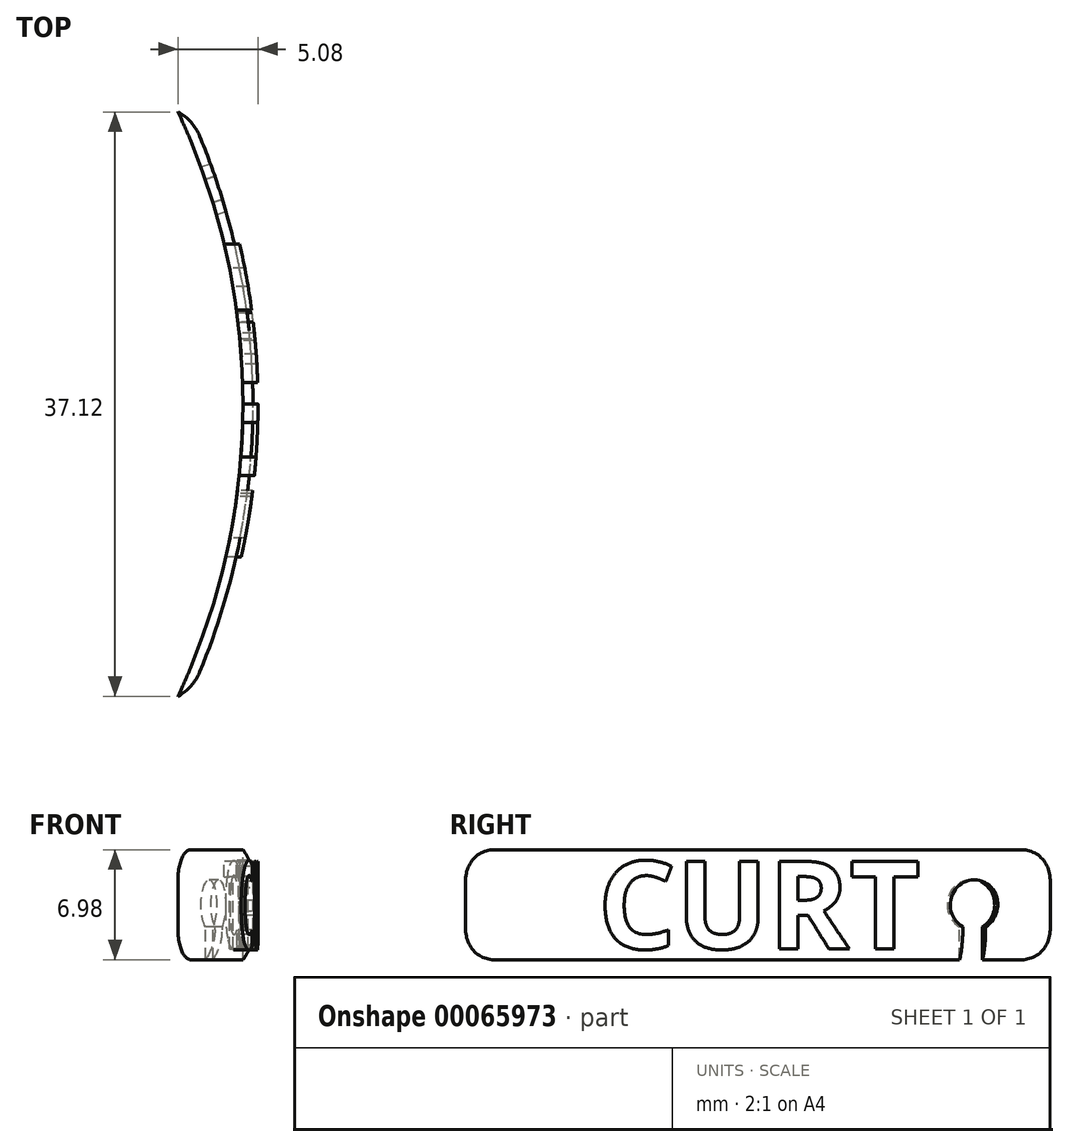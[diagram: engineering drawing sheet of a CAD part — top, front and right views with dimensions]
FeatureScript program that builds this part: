
annotation { "Feature Type Name" : "Feature", "Feature Type Description" : "" }
export const myFeature = defineFeature(function(context is Context, id is Id, definition is map)
    precondition{}
    {
        {
            var Q0;
            Q0=qCreatedBy(makeId("Front.planeOp"),FACE);
            var sketch = newSketch(context, id + "F0", { "sketchPlane" : qUnion([Q0])});
            skLineSegment(sketch, "E0", {"start": v(38.1, -1.59) * mm, "end": v(38.1, 1.59) * mm});
            skLineSegment(sketch, "E1", {"start": v(44.45, 1.59) * mm, "end": v(44.45, -1.59) * mm});
            skArc(sketch, "E2", {"start": v(44.45, 1.59) * mm, "mid": v(41.28, 4.76) * mm, "end": v(38.1, 1.59) * mm});
            skArc(sketch, "E3", {"start": v(38.1, -1.59) * mm, "mid": v(41.28, -4.76) * mm, "end": v(44.45, -1.59) * mm});
            skLineSegment(sketch, "E4", {"start": v(0, 0) * mm, "end": v(0, -27.8) * mm});
            skSolve(sketch);
        }
        {
            var Q0;
            Q0=makeQuery(id+"F0.imprint","IMPRINT",FACE,{"disambiguationData":[TD([[makeQuery(id+"F0.imprint","IMPRINT",EDGE,{"derivedFrom":sQuery(id+"F0.wireOp",EDGE,"E0")}),-1.0]])]});
            var Q1;
            Q1=sQuery(id+"F0.wireOp",EDGE,"E4");
            revolve(context, id + "F1", {"entities" : qUnion([Q0]), "axis" : qUnion([Q1]), "revolveType" : RevolveType.SYMMETRIC, "angle" : 45 * degree});
        }
        {
            var Q0;
            Q0=makeQuery(id+"F1.opRevolve","CAP_FACE",FACE,{"disambiguationData":[OSD([sQuery(id+"F0.wireOp",EDGE,"E0"),sQuery(id+"F0.wireOp",EDGE,"E1"),sQuery(id+"F0.wireOp",EDGE,"E2"),sQuery(id+"F0.wireOp",EDGE,"E3")])],"isStart":false});
            var sketch = newSketch(context, id + "F2", { "sketchPlane" : qUnion([Q0])});
            skLineSegment(sketch, "E5", {"start": v(41.28, 4.76) * mm, "end": v(41.28, -4.76) * mm});
            skSolve(sketch);
        }
        {
            var Q0;
            Q0 = qSketchRegion(id + "F2", true);
            var Q1;
            {var subQ0=sQuery(id+"F2.wireOp",EDGE,"E5");Q1=makeQuery(id+"F2.imprint","IMPRINT",FACE,{"disambiguationData":[TD([[makeQuery(id+"F2.imprint","IMPRINT",EDGE,{"derivedFrom":subQ0}),1.0]])]});}
            var Q2;
            Q2=sQuery(id+"F2.wireOp",EDGE,"E5");
            revolve(context, id + "F3", {"operationType" : NewBodyOperationType.ADD, "entities" : qUnion([Q0, Q1]), "axis" : qUnion([Q2]), "revolveType" : RevolveType.FULL});
        }
        {
            var Q0;
            Q0=makeQuery(id+"F1.opRevolve","CAP_FACE",FACE,{"disambiguationData":[OSD([sQuery(id+"F0.wireOp",EDGE,"E0"),sQuery(id+"F0.wireOp",EDGE,"E1"),sQuery(id+"F0.wireOp",EDGE,"E2"),sQuery(id+"F0.wireOp",EDGE,"E3")])],"isStart":true});
            var sketch = newSketch(context, id + "F4", { "sketchPlane" : qUnion([Q0])});
            skLineSegment(sketch, "E6", {"start": v(-41.28, 4.76) * mm, "end": v(-41.28, -4.76) * mm});
            skSolve(sketch);
        }
        {
            var Q0;
            Q0 = qSketchRegion(id + "F4", true);
            var Q1;
            {var subQ0=sQuery(id+"F4.wireOp",EDGE,"E6");Q1=makeQuery(id+"F4.imprint","IMPRINT",FACE,{"disambiguationData":[TD([[makeQuery(id+"F4.imprint","IMPRINT",EDGE,{"derivedFrom":subQ0}),1.0]])]});}
            var Q2;
            Q2=sQuery(id+"F4.wireOp",EDGE,"E6");
            revolve(context, id + "F5", {"operationType" : NewBodyOperationType.ADD, "entities" : qUnion([Q0, Q1]), "axis" : qUnion([Q2]), "revolveType" : RevolveType.FULL});
        }
        {
            var Q0;
            Q0=qCreatedBy(makeId("Front.planeOp"),FACE);
            var sketch = newSketch(context, id + "F6", { "sketchPlane" : qUnion([Q0])});
            skLineSegment(sketch, "E7", {"start": v(38.13, 4.76) * mm, "end": v(41.28, 4.76) * mm});
            skArc(sketch, "E8", {"start": v(41.28, 4.76) * mm, "mid": v(39.03, 3.83) * mm, "end": v(38.1, 1.59) * mm});
            skLineSegment(sketch, "E9", {"start": v(44.45, 1.59) * mm, "end": v(44.45, -1.59) * mm});
            skLineSegment(sketch, "E10", {"start": v(38.13, -4.76) * mm, "end": v(41.28, -4.76) * mm});
            skArc(sketch, "E11", {"start": v(38.1, -1.59) * mm, "mid": v(39.03, -3.83) * mm, "end": v(41.28, -4.76) * mm});
            skLineSegment(sketch, "E12", {"start": v(41.28, 4.76) * mm, "end": v(41.28, -4.76) * mm, "construction": true});
            skLineSegment(sketch, "E13", {"start": v(0, 0) * mm, "end": v(48.62, 0) * mm, "construction": true});
            skPoint(sketch, "E13.endSnap0", {"position": v(44.45, 0) * mm});
            skLineSegment(sketch, "E14", {"start": v(39.69, -6.35) * mm, "end": v(39.69, 0.76) * mm});
            skLineSegment(sketch, "E15", {"start": v(42.86, -6.35) * mm, "end": v(42.86, 0.76) * mm});
            skLineSegment(sketch, "E16", {"start": v(39.69, -6.35) * mm, "end": v(42.86, -6.35) * mm});
            skArc(sketch, "E17", {"start": v(42.86, 0.76) * mm, "mid": v(41.28, 2.35) * mm, "end": v(39.69, 0.76) * mm});
            skLineSegment(sketch, "E18", {"start": v(0, 0) * mm, "end": v(0, -11.33) * mm, "construction": true});
            skArc(sketch, "E19", {"start": v(39.69, -4.28) * mm, "mid": v(40, -2.76) * mm, "end": v(39.69, -1.23) * mm});
            skArc(sketch, "E20", {"start": v(42.86, -1.23) * mm, "mid": v(42.55, -2.76) * mm, "end": v(42.86, -4.28) * mm});
            skLineSegment(sketch, "E21", {"start": v(39.69, -1.23) * mm, "end": v(42.86, -1.23) * mm, "construction": true});
            skLineSegment(sketch, "E22", {"start": v(39.69, -4.28) * mm, "end": v(42.86, -4.28) * mm, "construction": true});
            skSolve(sketch);
        }
        {
            var Q0;
            {var subQ0=sQuery(id+"F6.wireOp",EDGE,"E11");var subQ1=sQuery(id+"F6.wireOp",EDGE,"E10");var subQ2=makeQuery(id+"F6.imprint","INTERSECT",VERTEX,{"derivedFrom":[subQ1,subQ0]});Q0=makeQuery(id+"F6.imprint","IMPRINT",FACE,{"disambiguationData":[TD([[makeQuery(id+"F6.imprint","IMPRINT",EDGE,{"disambiguationData":[TD([[subQ2,1.0]])],"derivedFrom":subQ1}),1.0]])]});}
            var Q1;
            Q1=makeQuery(id+"F6.imprint","IMPRINT",FACE,{"disambiguationData":[TD([[makeQuery(id+"F6.imprint","IMPRINT",EDGE,{"derivedFrom":sQuery(id+"F6.wireOp",EDGE,"E15")}),1.0]])]});
            var Q2;
            Q2=sQuery(id+"F6.wireOp",EDGE,"E18");
            revolve(context, id + "F7", {"operationType" : NewBodyOperationType.REMOVE, "entities" : qUnion([Q0, Q1]), "axis" : qUnion([Q2]), "revolveType" : RevolveType.FULL, "oppositeDirection" : true});
        }
        {
            var Q0;
            Q0=qCreatedBy(makeId("Top.planeOp"),FACE);
            var sketch = newSketch(context, id + "F8", { "sketchPlane" : qUnion([Q0])});
            skArc(sketch, "E23.0", {"start": v(41.07, -17.01) * mm, "mid": v(44.45, 0) * mm, "end": v(41.07, 17.01) * mm});
            skLineSegment(sketch, "E24.0", {"start": v(41.07, 17.01) * mm, "end": v(35.2, 14.58) * mm});
            skFitSpline(sketch, "E25.0", {"points": [v(35.7, 17.84) * mm, v(35.8, 17.96) * mm, v(35.96, 18.09) * mm, v(36.16, 18.22) * mm, v(36.37, 18.36) * mm, v(36.6, 18.48) * mm, v(36.85, 18.6) * mm, v(37.1, 18.72) * mm, v(37.35, 18.8) * mm, v(37.59, 18.87) * mm, v(37.82, 18.94) * mm, v(38.02, 18.97) * mm, v(38.18, 18.97) * mm]});
            skPoint(sketch, "E26.startSnap0", {"position": v(38.13, 15.8) * mm});
            skCircle(sketch, "E27", {"center": v(0, 0) * mm, "radius": 41.28 * mm, "construction": true});
            skLineSegment(sketch, "E28", {"start": v(0, 0) * mm, "end": v(47.07, 15.3) * mm, "construction": true});
            skArc(sketch, "E29", {"start": v(38.53, 12.52) * mm, "mid": v(37.01, 16.48) * mm, "end": v(35.09, 20.26) * mm});
            skArc(sketch, "E30", {"start": v(39.98, 13) * mm, "mid": v(38.4, 17.1) * mm, "end": v(36.4, 21.02) * mm});
            skArc(sketch, "E31", {"start": v(38.53, 12.52) * mm, "mid": v(39.5, 12.03) * mm, "end": v(39.98, 13) * mm});
            skLineSegment(sketch, "E32", {"start": v(35.09, 20.26) * mm, "end": v(36.4, 21.02) * mm});
            skSolve(sketch);
        }
        {
            var Q0;
            Q0 = qSketchRegion(id + "F8", true);
            extrude(context, id + "F9", {"entities" : qUnion([Q0]), "operationType" : NewBodyOperationType.REMOVE, "endBound" : BoundingType.THROUGH_ALL, "depth" : 25.4 * mm});
        }
        {
            var Q0;
            Q0=sQuery(id+"F8.wireOp",VERTEX,"E30.center");
            var Q1;
            Q1=sQuery(id+"F8.wireOp",EDGE,"E28");
            cPlane(context, id + "F10", {"entities" : qUnion([Q0, Q1]), "cplaneType" : CPlaneType.LINE_POINT, "offset" : 152.4 * mm, "width" : 152.4 * mm, "height" : 152.4 * mm});
        }
        {
            var Q0;
            Q0=qCreatedBy(id+"F10.planeOp",FACE);
            var sketch = newSketch(context, id + "F11", { "sketchPlane" : qUnion([Q0])});
            skPoint(sketch, "E33", {"position": v(0, 0) * mm});
            skSolve(sketch);
        }
        {
            var Q0;
            Q0=sQuery(id+"F11.wireOp",VERTEX,"E33");
            var Q1;
            Q1=makeQuery(id+"F1.opRevolve","SWEPT_BODY",BODY,{"disambiguationData":[OSD([sQuery(id+"F0.wireOp",EDGE,"E0"),sQuery(id+"F0.wireOp",EDGE,"E1"),sQuery(id+"F0.wireOp",EDGE,"E2"),sQuery(id+"F0.wireOp",EDGE,"E3")])]});
            hole(context, id + "F12", {"style" : HoleStyle.SIMPLE, "holeDiameter" : 3.17 * mm, "endStyle" : HoleEndStyle.THROUGH, "oppositeDirection" : true, "locations" : qUnion([Q0]), "scope" : qUnion([Q1])});
        }
        {
            var Q0;
            Q0=qCreatedBy(makeId("Top.planeOp"),FACE);
            var sketch = newSketch(context, id + "F13", { "sketchPlane" : qUnion([Q0])});
            skArc(sketch, "E34.0", {"start": v(38.53, 12.52) * mm, "mid": v(39.5, 12.03) * mm, "end": v(39.98, 13) * mm});
            skLineSegment(sketch, "E35", {"start": v(40.25, 14.75) * mm, "end": v(41.76, 15.24) * mm});
            skLineSegment(sketch, "E36", {"start": v(42.74, 12.22) * mm, "end": v(41.23, 11.73) * mm});
            skLineSegment(sketch, "E37", {"start": v(35.71, 13.27) * mm, "end": v(37.22, 13.76) * mm});
            skLineSegment(sketch, "E38", {"start": v(38.2, 10.74) * mm, "end": v(36.7, 10.25) * mm});
            skLineSegment(sketch, "E39", {"start": v(35.4, 12.3) * mm, "end": v(39.02, 13.48) * mm});
            skLineSegment(sketch, "E40", {"start": v(39.02, 13.48) * mm, "end": v(39.5, 12.03) * mm});
            skLineSegment(sketch, "E41", {"start": v(39.5, 12.03) * mm, "end": v(35.86, 10.85) * mm});
            skLineSegment(sketch, "E42", {"start": v(35.86, 10.85) * mm, "end": v(35.4, 12.3) * mm});
            skLineSegment(sketch, "E43", {"start": v(35.63, 11.58) * mm, "end": v(39.25, 12.75) * mm, "construction": true});
            skSolve(sketch);
        }
        {
            var Q0;
            Q0 = qSketchRegion(id + "F13", true);
            extrude(context, id + "F14", {"entities" : qUnion([Q0]), "operationType" : NewBodyOperationType.REMOVE, "endBound" : BoundingType.THROUGH_ALL, "depth" : 25.4 * mm});
        }
        {
            var Q0;
            Q0=qCreatedBy(makeId("Top.planeOp"),FACE);
            var sketch = newSketch(context, id + "F15", { "sketchPlane" : qUnion([Q0])});
            skLineSegment(sketch, "E44", {"start": v(39.02, 13.48) * mm, "end": v(39.5, 12.03) * mm});
            skLineSegment(sketch, "E45", {"start": v(39.5, 12.03) * mm, "end": v(43.11, 13.2) * mm});
            skLineSegment(sketch, "E46", {"start": v(43.11, 13.2) * mm, "end": v(42.64, 14.66) * mm});
            skLineSegment(sketch, "E47", {"start": v(42.64, 14.66) * mm, "end": v(39.02, 13.48) * mm});
            skSolve(sketch);
        }
        {
            var Q0;
            Q0 = qSketchRegion(id + "F15", true);
            extrude(context, id + "F16", {"entities" : qUnion([Q0]), "operationType" : NewBodyOperationType.REMOVE, "endBound" : BoundingType.THROUGH_ALL, "oppositeDirection" : true, "depth" : 25.4 * mm});
        }
        {
            var Q0;
            {var subQ0=sQuery(id+"F0.wireOp",EDGE,"E3");var subQ1=makeQuery(id+"F1.opRevolve","SWEPT_FACE",FACE,{"disambiguationData":[OSD([subQ0])]});var subQ2=sQuery(id+"F6.wireOp",EDGE,"E15");var subQ3=makeQuery(id+"F7.opRevolve","SWEPT_FACE",FACE,{"disambiguationData":[OSD([subQ2]),TDD([makeQuery(id+"F6.imprint","IMPRINT",EDGE,{"disambiguationData":[TD([[makeQuery(id+"F6.imprint","INTERSECT",VERTEX,{"derivedFrom":[subQ2,sQuery(id+"F6.wireOp",EDGE,"E16")]}),-1.0]])],"derivedFrom":subQ2})])]});Q0=makeQuery(id+"F16.boolean.opBoolean","SPLIT",EDGE,{"disambiguationData":[TD([makeQuery(id+"F3.opRevolve","SWEPT_FACE",FACE,{"disambiguationData":[OSD([subQ0])]})])],"derivedFrom":makeQuery(id+"F7.boolean.opBoolean","INTERSECT",EDGE,{"derivedFrom":[subQ1,subQ3]})});}
            var Q1;
            {var subQ0=sQuery(id+"F0.wireOp",EDGE,"E3");var subQ1=makeQuery(id+"F1.opRevolve","SWEPT_FACE",FACE,{"disambiguationData":[OSD([subQ0])]});var subQ2=sQuery(id+"F6.wireOp",EDGE,"E15");var subQ3=makeQuery(id+"F7.opRevolve","SWEPT_FACE",FACE,{"disambiguationData":[OSD([subQ2]),TDD([makeQuery(id+"F6.imprint","IMPRINT",EDGE,{"disambiguationData":[TD([[makeQuery(id+"F6.imprint","INTERSECT",VERTEX,{"derivedFrom":[subQ2,sQuery(id+"F6.wireOp",EDGE,"E16")]}),-1.0]])],"derivedFrom":subQ2})])]});Q1=makeQuery(id+"F16.boolean.opBoolean","SPLIT",EDGE,{"disambiguationData":[TD([makeQuery(id+"F5.opRevolve","SWEPT_FACE",FACE,{"disambiguationData":[OSD([subQ0])]})])],"derivedFrom":makeQuery(id+"F7.boolean.opBoolean","INTERSECT",EDGE,{"derivedFrom":[subQ1,subQ3]})});}
            var Q2;
            {var subQ0=sQuery(id+"F6.wireOp",EDGE,"E15");Q2=makeQuery(id+"F7.boolean.opBoolean","INTERSECT",EDGE,{"derivedFrom":[makeQuery(id+"F5.opRevolve","SWEPT_FACE",FACE,{"disambiguationData":[OSD([sQuery(id+"F0.wireOp",EDGE,"E3")])]}),makeQuery(id+"F7.opRevolve","SWEPT_FACE",FACE,{"disambiguationData":[OSD([subQ0]),TDD([makeQuery(id+"F6.imprint","IMPRINT",EDGE,{"disambiguationData":[TD([[makeQuery(id+"F6.imprint","INTERSECT",VERTEX,{"derivedFrom":[subQ0,sQuery(id+"F6.wireOp",EDGE,"E16")]}),-1.0]])],"derivedFrom":subQ0})])]})]});}
            var Q3;
            {var subQ0=sQuery(id+"F6.wireOp",EDGE,"E14");var subQ2=makeQuery(id+"F6.imprint","INTERSECT",VERTEX,{"derivedFrom":[sQuery(id+"F6.wireOp",EDGE,"E10"),subQ0]});Q3=makeQuery(id+"F7.boolean.opBoolean","INTERSECT",EDGE,{"derivedFrom":[makeQuery(id+"F5.opRevolve","SWEPT_FACE",FACE,{"disambiguationData":[OSD([sQuery(id+"F0.wireOp",EDGE,"E3")])]}),makeQuery(id+"F7.opRevolve","SWEPT_FACE",FACE,{"disambiguationData":[OSD([subQ0]),TDD([makeQuery(id+"F6.imprint","IMPRINT",EDGE,{"disambiguationData":[TD([[makeQuery(id+"F6.imprint","INTERSECT",VERTEX,{"derivedFrom":[subQ0,sQuery(id+"F6.wireOp",EDGE,"E16")]}),-1.0]])],"derivedFrom":subQ0}),makeQuery(id+"F6.imprint","IMPRINT",EDGE,{"disambiguationData":[TD([[subQ2,-1.0]])],"derivedFrom":subQ0}),makeQuery(id+"F6.imprint","IMPRINT",EDGE,{"disambiguationData":[TD([[makeQuery(id+"F6.imprint","INTERSECT",VERTEX,{"disambiguationData":[OD(0.0)],"derivedFrom":[subQ0,sQuery(id+"F6.wireOp",EDGE,"E19")]}),1.0]])],"derivedFrom":subQ0})])]})]});}
            var Q4;
            {var subQ0=sQuery(id+"F6.wireOp",EDGE,"E14");var subQ2=makeQuery(id+"F6.imprint","INTERSECT",VERTEX,{"derivedFrom":[sQuery(id+"F6.wireOp",EDGE,"E10"),subQ0]});Q4=makeQuery(id+"F7.boolean.opBoolean","INTERSECT",EDGE,{"derivedFrom":[makeQuery(id+"F1.opRevolve","SWEPT_FACE",FACE,{"disambiguationData":[OSD([sQuery(id+"F0.wireOp",EDGE,"E3")])]}),makeQuery(id+"F7.opRevolve","SWEPT_FACE",FACE,{"disambiguationData":[OSD([subQ0]),TDD([makeQuery(id+"F6.imprint","IMPRINT",EDGE,{"disambiguationData":[TD([[makeQuery(id+"F6.imprint","INTERSECT",VERTEX,{"derivedFrom":[subQ0,sQuery(id+"F6.wireOp",EDGE,"E16")]}),-1.0]])],"derivedFrom":subQ0}),makeQuery(id+"F6.imprint","IMPRINT",EDGE,{"disambiguationData":[TD([[subQ2,-1.0]])],"derivedFrom":subQ0}),makeQuery(id+"F6.imprint","IMPRINT",EDGE,{"disambiguationData":[TD([[makeQuery(id+"F6.imprint","INTERSECT",VERTEX,{"disambiguationData":[OD(0.0)],"derivedFrom":[subQ0,sQuery(id+"F6.wireOp",EDGE,"E19")]}),1.0]])],"derivedFrom":subQ0})])]})]});}
            var Q5;
            {var subQ0=sQuery(id+"F6.wireOp",EDGE,"E14");var subQ2=makeQuery(id+"F6.imprint","INTERSECT",VERTEX,{"derivedFrom":[sQuery(id+"F6.wireOp",EDGE,"E10"),subQ0]});Q5=makeQuery(id+"F7.boolean.opBoolean","INTERSECT",EDGE,{"derivedFrom":[makeQuery(id+"F3.opRevolve","SWEPT_FACE",FACE,{"disambiguationData":[OSD([sQuery(id+"F0.wireOp",EDGE,"E3")])]}),makeQuery(id+"F7.opRevolve","SWEPT_FACE",FACE,{"disambiguationData":[OSD([subQ0]),TDD([makeQuery(id+"F6.imprint","IMPRINT",EDGE,{"disambiguationData":[TD([[makeQuery(id+"F6.imprint","INTERSECT",VERTEX,{"derivedFrom":[subQ0,sQuery(id+"F6.wireOp",EDGE,"E16")]}),-1.0]])],"derivedFrom":subQ0}),makeQuery(id+"F6.imprint","IMPRINT",EDGE,{"disambiguationData":[TD([[subQ2,-1.0]])],"derivedFrom":subQ0}),makeQuery(id+"F6.imprint","IMPRINT",EDGE,{"disambiguationData":[TD([[makeQuery(id+"F6.imprint","INTERSECT",VERTEX,{"disambiguationData":[OD(0.0)],"derivedFrom":[subQ0,sQuery(id+"F6.wireOp",EDGE,"E19")]}),1.0]])],"derivedFrom":subQ0})])]})]});}
            var Q6;
            {var subQ0=sQuery(id+"F6.wireOp",EDGE,"E15");Q6=makeQuery(id+"F7.boolean.opBoolean","INTERSECT",EDGE,{"derivedFrom":[makeQuery(id+"F3.opRevolve","SWEPT_FACE",FACE,{"disambiguationData":[OSD([sQuery(id+"F0.wireOp",EDGE,"E3")])]}),makeQuery(id+"F7.opRevolve","SWEPT_FACE",FACE,{"disambiguationData":[OSD([subQ0]),TDD([makeQuery(id+"F6.imprint","IMPRINT",EDGE,{"disambiguationData":[TD([[makeQuery(id+"F6.imprint","INTERSECT",VERTEX,{"derivedFrom":[subQ0,sQuery(id+"F6.wireOp",EDGE,"E16")]}),-1.0]])],"derivedFrom":subQ0})])]})]});}
            var Q7;
            Q7=makeQuery(id+"F7.boolean.opBoolean","INTERSECT",EDGE,{"derivedFrom":[makeQuery(id+"F3.opRevolve","SWEPT_FACE",FACE,{"disambiguationData":[OSD([sQuery(id+"F0.wireOp",EDGE,"E3")])]}),makeQuery(id+"F7.opRevolve","SWEPT_FACE",FACE,{"disambiguationData":[OSD([sQuery(id+"F6.wireOp",EDGE,"E20")])]})]});
            var Q8;
            Q8=makeQuery(id+"F7.boolean.opBoolean","INTERSECT",EDGE,{"derivedFrom":[makeQuery(id+"F3.opRevolve","SWEPT_FACE",FACE,{"disambiguationData":[OSD([sQuery(id+"F0.wireOp",EDGE,"E1")])]}),makeQuery(id+"F7.opRevolve","SWEPT_FACE",FACE,{"disambiguationData":[OSD([sQuery(id+"F6.wireOp",EDGE,"E20")])]})]});
            var Q9;
            {var subQ0=sQuery(id+"F6.wireOp",EDGE,"E15");Q9=makeQuery(id+"F7.boolean.opBoolean","INTERSECT",EDGE,{"derivedFrom":[makeQuery(id+"F3.opRevolve","SWEPT_FACE",FACE,{"disambiguationData":[OSD([sQuery(id+"F0.wireOp",EDGE,"E1")])]}),makeQuery(id+"F7.opRevolve","SWEPT_FACE",FACE,{"disambiguationData":[OSD([subQ0]),TDD([makeQuery(id+"F6.imprint","IMPRINT",EDGE,{"disambiguationData":[TD([[makeQuery(id+"F6.imprint","INTERSECT",VERTEX,{"derivedFrom":[subQ0,sQuery(id+"F6.wireOp",EDGE,"E17")]}),1.0]])],"derivedFrom":subQ0})])]})]});}
            var Q10;
            Q10=makeQuery(id+"F7.boolean.opBoolean","INTERSECT",EDGE,{"disambiguationData":[OD(1.0)],"derivedFrom":[makeQuery(id+"F3.opRevolve","SWEPT_FACE",FACE,{"disambiguationData":[OSD([sQuery(id+"F0.wireOp",EDGE,"E1")])]}),makeQuery(id+"F7.opRevolve","SWEPT_FACE",FACE,{"disambiguationData":[OSD([sQuery(id+"F6.wireOp",EDGE,"E17")])]})]});
            var Q11;
            Q11=makeQuery(id+"F7.boolean.opBoolean","INTERSECT",EDGE,{"derivedFrom":[makeQuery(id+"F3.opRevolve","SWEPT_FACE",FACE,{"disambiguationData":[OSD([sQuery(id+"F0.wireOp",EDGE,"E2")])]}),makeQuery(id+"F7.opRevolve","SWEPT_FACE",FACE,{"disambiguationData":[OSD([sQuery(id+"F6.wireOp",EDGE,"E17")])]})]});
            var Q12;
            Q12=makeQuery(id+"F7.boolean.opBoolean","INTERSECT",EDGE,{"disambiguationData":[OD(0.0)],"derivedFrom":[makeQuery(id+"F3.opRevolve","SWEPT_FACE",FACE,{"disambiguationData":[OSD([sQuery(id+"F0.wireOp",EDGE,"E1")])]}),makeQuery(id+"F7.opRevolve","SWEPT_FACE",FACE,{"disambiguationData":[OSD([sQuery(id+"F6.wireOp",EDGE,"E17")])]})]});
            var Q13;
            {var subQ0=sQuery(id+"F6.wireOp",EDGE,"E14");Q13=makeQuery(id+"F7.boolean.opBoolean","INTERSECT",EDGE,{"derivedFrom":[makeQuery(id+"F3.opRevolve","SWEPT_FACE",FACE,{"disambiguationData":[OSD([sQuery(id+"F0.wireOp",EDGE,"E1")])]}),makeQuery(id+"F7.opRevolve","SWEPT_FACE",FACE,{"disambiguationData":[OSD([subQ0]),TDD([makeQuery(id+"F6.imprint","IMPRINT",EDGE,{"disambiguationData":[TD([[makeQuery(id+"F6.imprint","INTERSECT",VERTEX,{"derivedFrom":[subQ0,sQuery(id+"F6.wireOp",EDGE,"E17")]}),1.0]])],"derivedFrom":subQ0})])]})]});}
            var Q14;
            Q14=makeQuery(id+"F7.boolean.opBoolean","INTERSECT",EDGE,{"derivedFrom":[makeQuery(id+"F3.opRevolve","SWEPT_FACE",FACE,{"disambiguationData":[OSD([sQuery(id+"F0.wireOp",EDGE,"E1")])]}),makeQuery(id+"F7.opRevolve","SWEPT_FACE",FACE,{"disambiguationData":[OSD([sQuery(id+"F6.wireOp",EDGE,"E19")])]})]});
            var Q15;
            Q15=makeQuery(id+"F7.boolean.opBoolean","INTERSECT",EDGE,{"derivedFrom":[makeQuery(id+"F3.opRevolve","SWEPT_FACE",FACE,{"disambiguationData":[OSD([sQuery(id+"F0.wireOp",EDGE,"E3")])]}),makeQuery(id+"F7.opRevolve","SWEPT_FACE",FACE,{"disambiguationData":[OSD([sQuery(id+"F6.wireOp",EDGE,"E19")])]})]});
            var Q16;
            Q16=makeQuery(id+"F7.boolean.opBoolean","INTERSECT",EDGE,{"derivedFrom":[makeQuery(id+"F5.opRevolve","SWEPT_FACE",FACE,{"disambiguationData":[OSD([sQuery(id+"F0.wireOp",EDGE,"E3")])]}),makeQuery(id+"F7.opRevolve","SWEPT_FACE",FACE,{"disambiguationData":[OSD([sQuery(id+"F6.wireOp",EDGE,"E19")])]})]});
            var Q17;
            Q17=makeQuery(id+"F7.boolean.opBoolean","INTERSECT",EDGE,{"derivedFrom":[makeQuery(id+"F5.opRevolve","SWEPT_FACE",FACE,{"disambiguationData":[OSD([sQuery(id+"F0.wireOp",EDGE,"E0")])]}),makeQuery(id+"F7.opRevolve","SWEPT_FACE",FACE,{"disambiguationData":[OSD([sQuery(id+"F6.wireOp",EDGE,"E19")])]})]});
            var Q18;
            {var subQ0=sQuery(id+"F6.wireOp",EDGE,"E14");Q18=makeQuery(id+"F7.boolean.opBoolean","INTERSECT",EDGE,{"derivedFrom":[makeQuery(id+"F5.opRevolve","SWEPT_FACE",FACE,{"disambiguationData":[OSD([sQuery(id+"F0.wireOp",EDGE,"E0")])]}),makeQuery(id+"F7.opRevolve","SWEPT_FACE",FACE,{"disambiguationData":[OSD([subQ0]),TDD([makeQuery(id+"F6.imprint","IMPRINT",EDGE,{"disambiguationData":[TD([[makeQuery(id+"F6.imprint","INTERSECT",VERTEX,{"derivedFrom":[subQ0,sQuery(id+"F6.wireOp",EDGE,"E17")]}),1.0]])],"derivedFrom":subQ0})])]})]});}
            var Q19;
            Q19=makeQuery(id+"F7.boolean.opBoolean","INTERSECT",EDGE,{"derivedFrom":[makeQuery(id+"F5.opRevolve","SWEPT_FACE",FACE,{"disambiguationData":[OSD([sQuery(id+"F0.wireOp",EDGE,"E3")])]}),makeQuery(id+"F7.opRevolve","SWEPT_FACE",FACE,{"disambiguationData":[OSD([sQuery(id+"F6.wireOp",EDGE,"E20")])]})]});
            var Q20;
            Q20=makeQuery(id+"F7.boolean.opBoolean","INTERSECT",EDGE,{"derivedFrom":[makeQuery(id+"F5.opRevolve","SWEPT_FACE",FACE,{"disambiguationData":[OSD([sQuery(id+"F0.wireOp",EDGE,"E0")])]}),makeQuery(id+"F7.opRevolve","SWEPT_FACE",FACE,{"disambiguationData":[OSD([sQuery(id+"F6.wireOp",EDGE,"E20")])]})]});
            var Q21;
            {var subQ0=sQuery(id+"F6.wireOp",EDGE,"E15");Q21=makeQuery(id+"F7.boolean.opBoolean","INTERSECT",EDGE,{"derivedFrom":[makeQuery(id+"F5.opRevolve","SWEPT_FACE",FACE,{"disambiguationData":[OSD([sQuery(id+"F0.wireOp",EDGE,"E0")])]}),makeQuery(id+"F7.opRevolve","SWEPT_FACE",FACE,{"disambiguationData":[OSD([subQ0]),TDD([makeQuery(id+"F6.imprint","IMPRINT",EDGE,{"disambiguationData":[TD([[makeQuery(id+"F6.imprint","INTERSECT",VERTEX,{"derivedFrom":[subQ0,sQuery(id+"F6.wireOp",EDGE,"E17")]}),1.0]])],"derivedFrom":subQ0})])]})]});}
            var Q22;
            Q22=makeQuery(id+"F7.boolean.opBoolean","INTERSECT",EDGE,{"disambiguationData":[OD(1.0)],"derivedFrom":[makeQuery(id+"F5.opRevolve","SWEPT_FACE",FACE,{"disambiguationData":[OSD([sQuery(id+"F0.wireOp",EDGE,"E0")])]}),makeQuery(id+"F7.opRevolve","SWEPT_FACE",FACE,{"disambiguationData":[OSD([sQuery(id+"F6.wireOp",EDGE,"E17")])]})]});
            var Q23;
            {var subQ0=makeQuery(id+"F5.opRevolve","SWEPT_FACE",FACE,{"disambiguationData":[OSD([sQuery(id+"F0.wireOp",EDGE,"E2")])]});var subQ1=makeQuery(id+"F7.opRevolve","SWEPT_FACE",FACE,{"disambiguationData":[OSD([sQuery(id+"F6.wireOp",EDGE,"E17")])]});Q23=makeQuery(id+"F9.boolean.opBoolean","SPLIT",EDGE,{"disambiguationData":[TD([makeQuery(id+"F9.opExtrude","SWEPT_FACE",FACE,{"disambiguationData":[OSD([sQuery(id+"F8.wireOp",EDGE,"E30")])]})])],"derivedFrom":makeQuery(id+"F7.boolean.opBoolean","INTERSECT",EDGE,{"derivedFrom":[subQ0,subQ1]})});}
            var Q24;
            Q24=makeQuery(id+"F7.boolean.opBoolean","INTERSECT",EDGE,{"disambiguationData":[OD(0.0)],"derivedFrom":[makeQuery(id+"F5.opRevolve","SWEPT_FACE",FACE,{"disambiguationData":[OSD([sQuery(id+"F0.wireOp",EDGE,"E0")])]}),makeQuery(id+"F7.opRevolve","SWEPT_FACE",FACE,{"disambiguationData":[OSD([sQuery(id+"F6.wireOp",EDGE,"E17")])]})]});
            var Q25;
            {var subQ0=makeQuery(id+"F5.opRevolve","SWEPT_FACE",FACE,{"disambiguationData":[OSD([sQuery(id+"F0.wireOp",EDGE,"E2")])]});var subQ1=makeQuery(id+"F7.opRevolve","SWEPT_FACE",FACE,{"disambiguationData":[OSD([sQuery(id+"F6.wireOp",EDGE,"E17")])]});Q25=makeQuery(id+"F9.boolean.opBoolean","SPLIT",EDGE,{"disambiguationData":[TD([makeQuery(id+"F9.opExtrude","SWEPT_FACE",FACE,{"disambiguationData":[OSD([sQuery(id+"F8.wireOp",EDGE,"E29")])]})])],"derivedFrom":makeQuery(id+"F7.boolean.opBoolean","INTERSECT",EDGE,{"derivedFrom":[subQ0,subQ1]})});}
            fillet(context, id + "F17", {"entities" : qUnion([Q0, Q1, Q2, Q3, Q4, Q5, Q6, Q7, Q8, Q9, Q10, Q11, Q12, Q13, Q14, Q15, Q16, Q17, Q18, Q19, Q20, Q21, Q22, Q23, Q24, Q25]), "radius" : 0.3 * mm, "allowEdgeOverflow" : false});
        }
        {
            var Q0;
            Q0=qCreatedBy(makeId("Right.planeOp"),FACE);
            cPlane(context, id + "F18", {"entities" : qUnion([Q0]), "cplaneType" : CPlaneType.OFFSET, "offset" : 44.45 * mm, "width" : 152.4 * mm, "height" : 152.4 * mm});
        }
        {
            var Q0;
            Q0=qCreatedBy(id+"F18.planeOp",FACE);
            var sketch = newSketch(context, id + "F19", { "sketchPlane" : qUnion([Q0])});
            skText(sketch, "E48", { "text": "CURT", "fontName": "OpenSans-Bold.ttf"});
            const initialGuessF19  = {"E48": [-0.01016, -0.0028, 1, 0, 0.0056]};
            skSetInitialGuess(sketch, initialGuessF19);
            skSolve(sketch);
        }
        {
            var Q0;
            Q0=makeQuery(id+"F19.imprint","IMPRINT",FACE,{"disambiguationData":[TD([[makeQuery(id+"F19.imprint","IMPRINT",EDGE,{"derivedFrom":sQuery(id+"F19.wireOp",EDGE,"E48.sketch_text.stroke-0")}),-1.0]])]});
            var Q1;
            Q1=makeQuery(id+"F19.imprint","IMPRINT",FACE,{"disambiguationData":[TD([[makeQuery(id+"F19.imprint","IMPRINT",EDGE,{"derivedFrom":sQuery(id+"F19.wireOp",EDGE,"E48.sketch_text.stroke-15")}),-1.0]])]});
            var Q2;
            Q2=makeQuery(id+"F19.imprint","IMPRINT",FACE,{"disambiguationData":[TD([[makeQuery(id+"F19.imprint","IMPRINT",EDGE,{"derivedFrom":sQuery(id+"F19.wireOp",EDGE,"E48.sketch_text.stroke-30")}),-1.0]])]});
            var Q3;
            Q3=makeQuery(id+"F19.imprint","IMPRINT",FACE,{"disambiguationData":[TD([[makeQuery(id+"F19.imprint","IMPRINT",EDGE,{"derivedFrom":sQuery(id+"F19.wireOp",EDGE,"E48.sketch_text.stroke-49")}),-1.0]])]});
            extrude(context, id + "F20", {"entities" : qUnion([Q0, Q1, Q2, Q3]), "endBound" : BoundingType.SYMMETRIC, "depth" : 25.4 * mm});
        }
        {
            var Q0;
            Q0=qCreatedBy(makeId("Top.planeOp"),FACE);
            var sketch = newSketch(context, id + "F21", { "sketchPlane" : qUnion([Q0])});
            skCircle(sketch, "E49", {"center": v(0, 0) * mm, "radius": 43.82 * mm});
            skCircle(sketch, "E50", {"center": v(0, 0) * mm, "radius": 44.77 * mm});
            skSolve(sketch);
        }
        {
            var Q0;
            Q0 = qSketchRegion(id + "F21", true);
            extrude(context, id + "F22", {"entities" : qUnion([Q0]), "operationType" : NewBodyOperationType.INTERSECT, "endBound" : BoundingType.SYMMETRIC, "oppositeDirection" : true, "depth" : 25.4 * mm});
        }
    });
